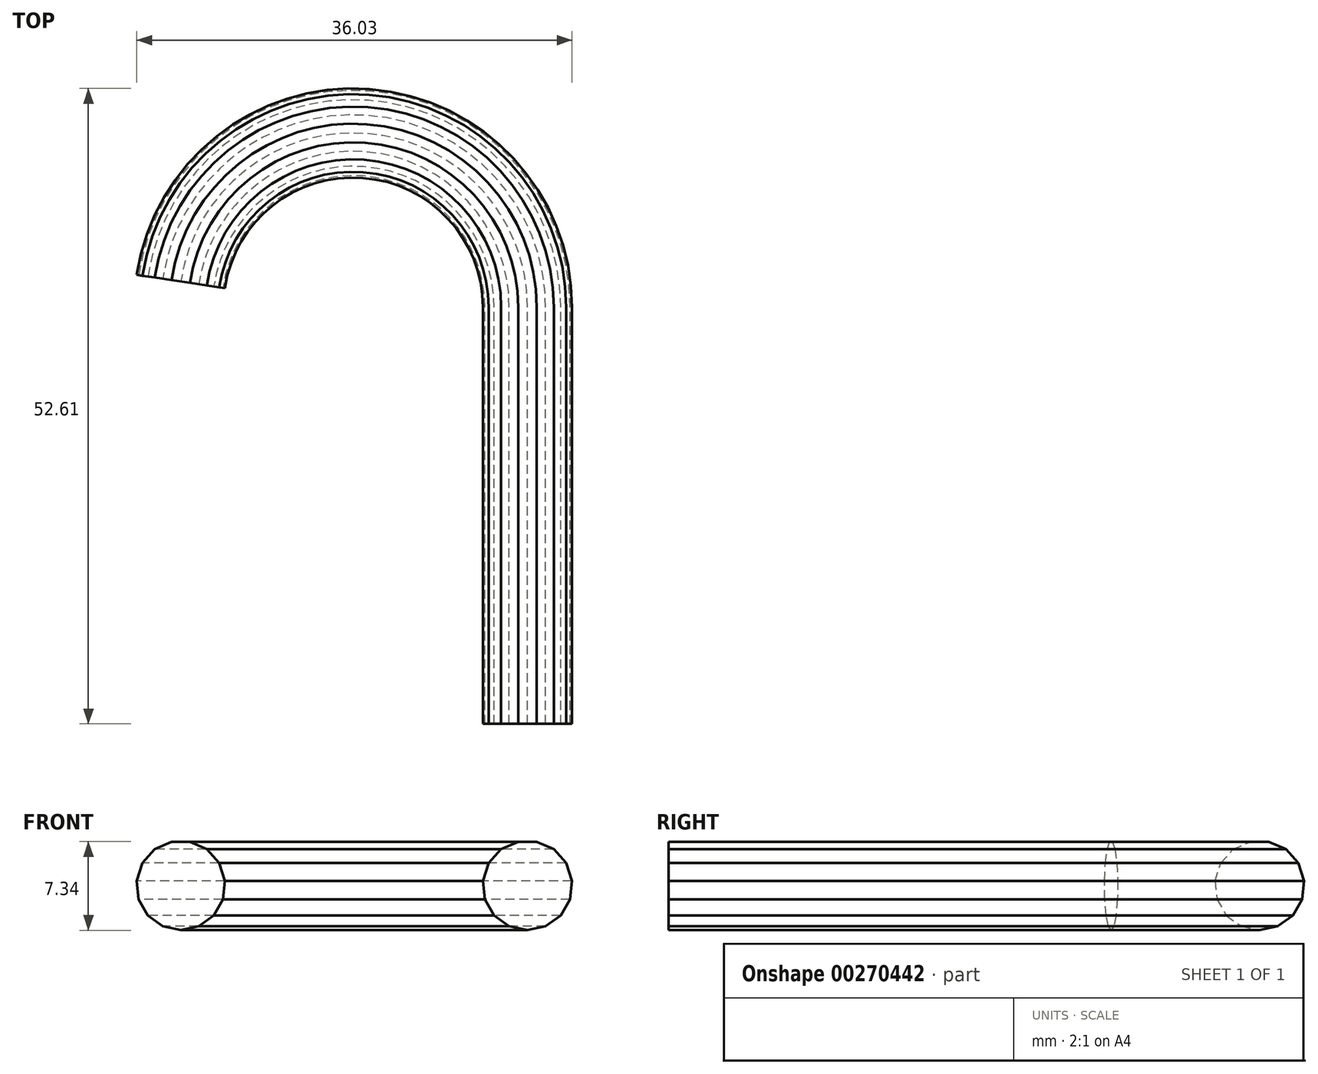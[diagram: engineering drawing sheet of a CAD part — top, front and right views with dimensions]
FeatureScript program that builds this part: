
annotation { "Feature Type Name" : "Feature", "Feature Type Description" : "" }
export const myFeature = defineFeature(function(context is Context, id is Id, definition is map)
    precondition{}
    {
        {
            var Q0;
            Q0=qCreatedBy(makeId("Top.planeOp"),FACE);
            var sketch = newSketch(context, id + "F0", { "sketchPlane" : qUnion([Q0])});
            skLineSegment(sketch, "E0", {"start": v(0, 0) * mm, "end": v(0, 34.5) * mm});
            skArc(sketch, "E1", {"start": v(0, 34.5) * mm, "mid": v(-13.36, 48.88) * mm, "end": v(-28.7, 36.63) * mm});
            skSolve(sketch);
        }
        {
            var Q0;
            Q0=qCreatedBy(makeId("Front.planeOp"),FACE);
            var sketch = newSketch(context, id + "F1", { "sketchPlane" : qUnion([Q0])});
            skCircle(sketch, "E2.cCircle", {"center": v(0, 0) * mm, "radius": 3.63 * mm, "construction": true});
            skLineSegment(sketch, "E2.0", {"start": v(-0.77, 3.63) * mm, "end": v(0.77, 3.63) * mm});
            skLineSegment(sketch, "E2.1", {"start": v(0.77, 3.63) * mm, "end": v(2.18, 3) * mm});
            skLineSegment(sketch, "E2.2", {"start": v(2.18, 3) * mm, "end": v(3.2, 1.85) * mm});
            skLineSegment(sketch, "E2.3", {"start": v(3.2, 1.85) * mm, "end": v(3.69, 0.39) * mm});
            skLineSegment(sketch, "E2.4", {"start": v(3.69, 0.39) * mm, "end": v(3.52, -1.15) * mm});
            skLineSegment(sketch, "E2.5", {"start": v(3.52, -1.15) * mm, "end": v(2.75, -2.48) * mm});
            skLineSegment(sketch, "E2.6", {"start": v(2.75, -2.48) * mm, "end": v(1.5, -3.39) * mm});
            skLineSegment(sketch, "E2.7", {"start": v(1.5, -3.39) * mm, "end": v(0, -3.7) * mm});
            skLineSegment(sketch, "E2.8", {"start": v(0, -3.7) * mm, "end": v(-1.5, -3.39) * mm});
            skLineSegment(sketch, "E2.9", {"start": v(-1.5, -3.39) * mm, "end": v(-2.75, -2.48) * mm});
            skLineSegment(sketch, "E2.10", {"start": v(-2.75, -2.48) * mm, "end": v(-3.52, -1.15) * mm});
            skLineSegment(sketch, "E2.11", {"start": v(-3.52, -1.15) * mm, "end": v(-3.69, 0.39) * mm});
            skLineSegment(sketch, "E2.12", {"start": v(-3.69, 0.39) * mm, "end": v(-3.2, 1.85) * mm});
            skLineSegment(sketch, "E2.13", {"start": v(-3.2, 1.85) * mm, "end": v(-2.18, 3) * mm});
            skLineSegment(sketch, "E2.14", {"start": v(-2.18, 3) * mm, "end": v(-0.77, 3.63) * mm});
            skPoint(sketch, "E2.0.midPoint", {"position": v(0, 3.63) * mm});
            skSolve(sketch);
        }
        {
            var Q0;
            Q0=makeQuery(id+"F1.imprint","IMPRINT",FACE,{"disambiguationData":[TD([[makeQuery(id+"F1.imprint","IMPRINT",EDGE,{"derivedFrom":sQuery(id+"F1.wireOp",EDGE,"E2.0")}),-1.0]])]});
            var Q1;
            Q1=sQuery(id+"F0.wireOp",EDGE,"E0");
            var Q2;
            Q2=sQuery(id+"F0.wireOp",EDGE,"E1");
            sweep(context, id + "F2", {"profiles" : qUnion([Q0]), "path" : qUnion([Q1, Q2])});
        }
    });
